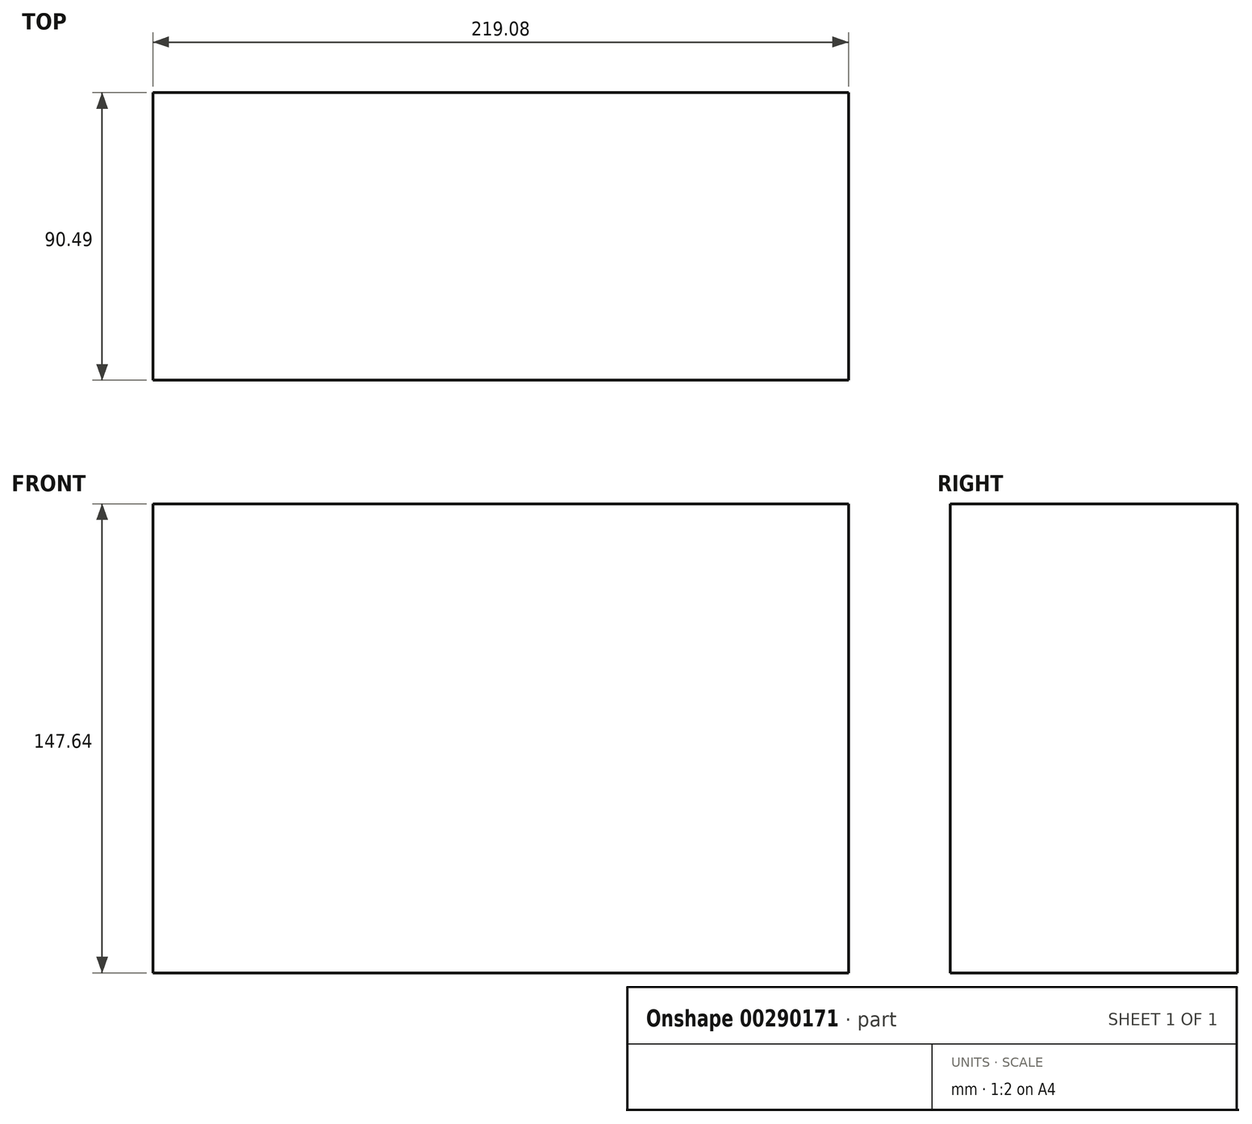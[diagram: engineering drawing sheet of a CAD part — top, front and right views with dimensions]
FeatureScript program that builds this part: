
annotation { "Feature Type Name" : "Feature", "Feature Type Description" : "" }
export const myFeature = defineFeature(function(context is Context, id is Id, definition is map)
    precondition{}
    {
        {
            var Q0;
            Q0=qCreatedBy(makeId("Front.planeOp"),FACE);
            var sketch = newSketch(context, id + "F0", { "sketchPlane" : qUnion([Q0])});
            skLineSegment(sketch, "E0.bottom", {"start": v(109.54, 73.82) * mm, "end": v(-109.54, 73.82) * mm});
            skLineSegment(sketch, "E0.top", {"start": v(109.54, -73.82) * mm, "end": v(-109.54, -73.82) * mm});
            skLineSegment(sketch, "E0.left", {"start": v(109.54, 73.82) * mm, "end": v(109.54, -73.82) * mm});
            skLineSegment(sketch, "E0.right", {"start": v(-109.54, 73.82) * mm, "end": v(-109.54, -73.82) * mm});
            skPoint(sketch, "E0.middle", {"position": v(0, 0) * mm});
            skSolve(sketch);
        }
        {
            var Q0;
            Q0 = qSketchRegion(id + "F0", true);
            extrude(context, id + "F1", {"entities" : qUnion([Q0]), "depth" : 90.49 * mm});
        }
    });
